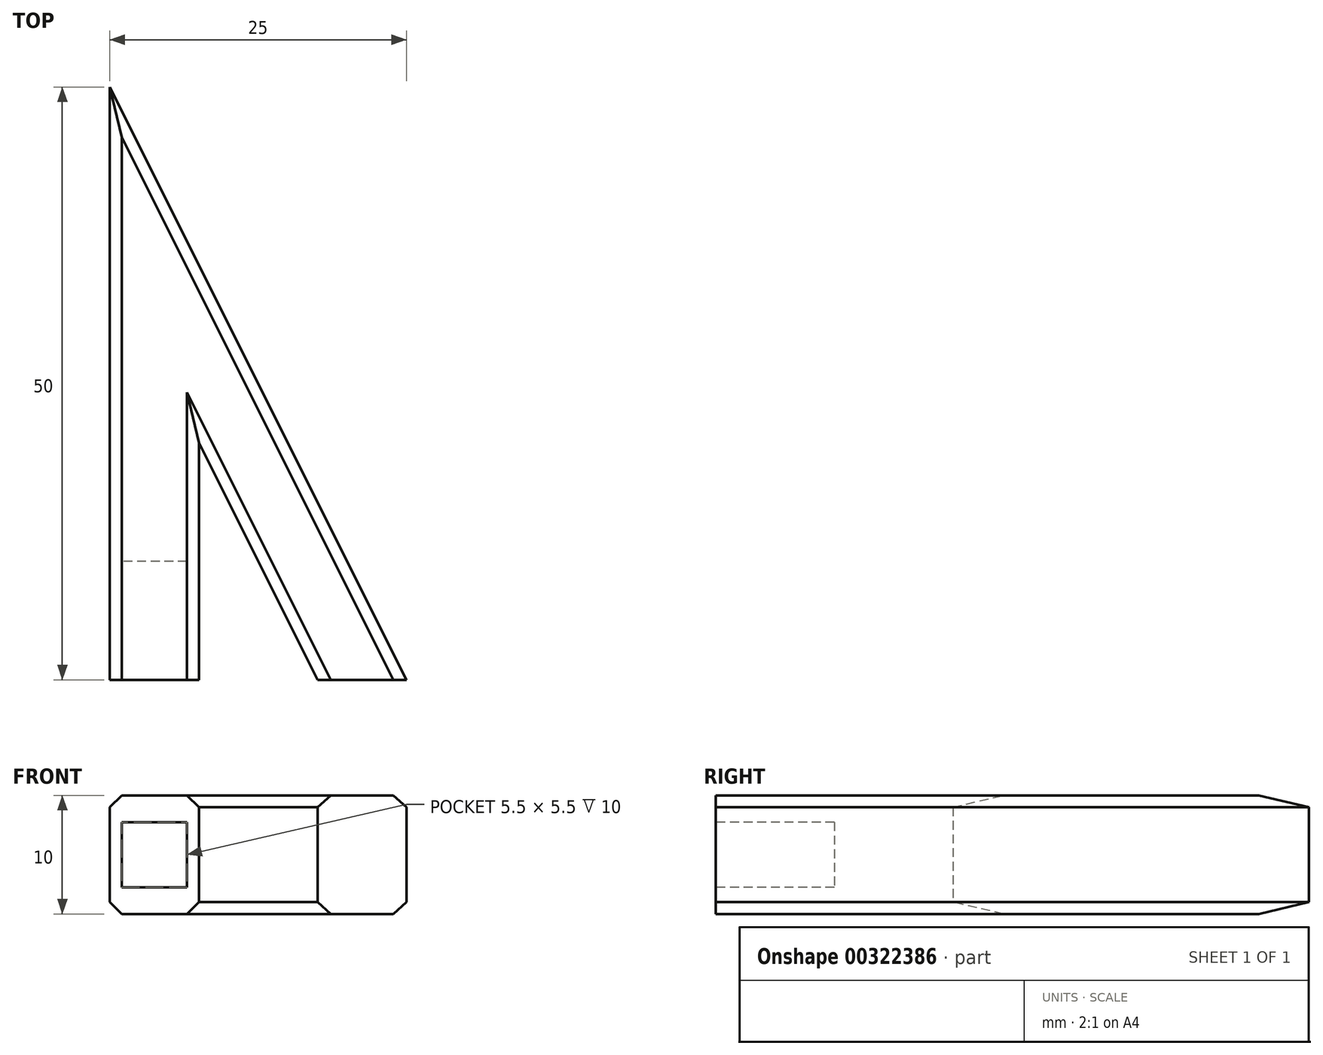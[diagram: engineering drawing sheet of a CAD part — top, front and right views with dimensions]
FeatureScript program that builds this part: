
annotation { "Feature Type Name" : "Feature", "Feature Type Description" : "" }
export const myFeature = defineFeature(function(context is Context, id is Id, definition is map)
    precondition{}
    {
        {
            var Q0;
            Q0=qCreatedBy(makeId("Top.planeOp"),FACE);
            var sketch = newSketch(context, id + "F0", { "sketchPlane" : qUnion([Q0])});
            skLineSegment(sketch, "E0", {"start": v(0, 0) * mm, "end": v(0, 50) * mm});
            skLineSegment(sketch, "E1", {"start": v(0, 50) * mm, "end": v(25, 0) * mm});
            skLineSegment(sketch, "E2", {"start": v(25, 0) * mm, "end": v(17.5, 0) * mm});
            skLineSegment(sketch, "E3", {"start": v(17.5, 0) * mm, "end": v(7.5, 20) * mm});
            skLineSegment(sketch, "E4", {"start": v(7.5, 20) * mm, "end": v(7.5, 0) * mm});
            skLineSegment(sketch, "E5.trimOffspring", {"start": v(7.5, 0) * mm, "end": v(0, 0) * mm});
            skSolve(sketch);
        }
        {
            var Q0;
            Q0=makeQuery(id+"F0.imprint","IMPRINT",FACE,{"disambiguationData":[TD([[makeQuery(id+"F0.imprint","IMPRINT",EDGE,{"derivedFrom":sQuery(id+"F0.wireOp",EDGE,"E0")}),-1.0]])]});
            extrude(context, id + "F1", {"entities" : qUnion([Q0]), "depth" : 10 * mm});
        }
        {
            var Q0;
            Q0=makeQuery(id+"F1.opExtrude","CAP_EDGE",EDGE,{"disambiguationData":[OSD([sQuery(id+"F0.wireOp",EDGE,"E3")])],"isStart":false});
            var Q1;
            Q1=makeQuery(id+"F1.opExtrude","CAP_EDGE",EDGE,{"disambiguationData":[OSD([sQuery(id+"F0.wireOp",EDGE,"E4")])],"isStart":false});
            var Q2;
            Q2=makeQuery(id+"F1.opExtrude","CAP_EDGE",EDGE,{"disambiguationData":[OSD([sQuery(id+"F0.wireOp",EDGE,"E0")])],"isStart":false});
            var Q3;
            Q3=makeQuery(id+"F1.opExtrude","CAP_EDGE",EDGE,{"disambiguationData":[OSD([sQuery(id+"F0.wireOp",EDGE,"E1")])],"isStart":false});
            var Q4;
            Q4=makeQuery(id+"F1.opExtrude","CAP_EDGE",EDGE,{"disambiguationData":[OSD([sQuery(id+"F0.wireOp",EDGE,"E3")])],"isStart":true});
            var Q5;
            Q5=makeQuery(id+"F1.opExtrude","CAP_EDGE",EDGE,{"disambiguationData":[OSD([sQuery(id+"F0.wireOp",EDGE,"E4")])],"isStart":true});
            var Q6;
            Q6=makeQuery(id+"F1.opExtrude","CAP_EDGE",EDGE,{"disambiguationData":[OSD([sQuery(id+"F0.wireOp",EDGE,"E0")])],"isStart":true});
            var Q7;
            Q7=makeQuery(id+"F1.opExtrude","CAP_EDGE",EDGE,{"disambiguationData":[OSD([sQuery(id+"F0.wireOp",EDGE,"E1")])],"isStart":true});
            chamfer(context, id + "F2", {"entities" : qUnion([Q0, Q1, Q2, Q3, Q4, Q5, Q6, Q7]), "width" : 1 * mm, "tangentPropagation" : true});
        }
        {
            var Q0;
            Q0=makeQuery(id+"F1.opExtrude","SWEPT_FACE",FACE,{"disambiguationData":[OSD([sQuery(id+"F0.wireOp",EDGE,"E5.trimOffspring")])]});
            var sketch = newSketch(context, id + "F3", { "sketchPlane" : qUnion([Q0])});
            skLineSegment(sketch, "E6", {"start": v(3.75, 10) * mm, "end": v(3.75, 0) * mm, "construction": true});
            skLineSegment(sketch, "E7", {"start": v(7.5, 5) * mm, "end": v(0, 5) * mm, "construction": true});
            skLineSegment(sketch, "E8.bottom", {"start": v(6.5, 7.75) * mm, "end": v(1, 7.75) * mm});
            skLineSegment(sketch, "E8.top", {"start": v(6.5, 2.25) * mm, "end": v(1, 2.25) * mm});
            skLineSegment(sketch, "E8.left", {"start": v(6.5, 7.75) * mm, "end": v(6.5, 2.25) * mm});
            skLineSegment(sketch, "E8.right", {"start": v(1, 7.75) * mm, "end": v(1, 2.25) * mm});
            skPoint(sketch, "E8.middle", {"position": v(3.75, 5) * mm});
            skSolve(sketch);
        }
        {
            var Q0;
            Q0=makeQuery(id+"F3.imprint","IMPRINT",FACE,{"disambiguationData":[TD([[makeQuery(id+"F3.imprint","IMPRINT",EDGE,{"derivedFrom":sQuery(id+"F3.wireOp",EDGE,"E8.bottom")}),1.0]])]});
            extrude(context, id + "F4", {"entities" : qUnion([Q0]), "operationType" : NewBodyOperationType.REMOVE, "oppositeDirection" : true, "depth" : 10 * mm});
        }
    });
